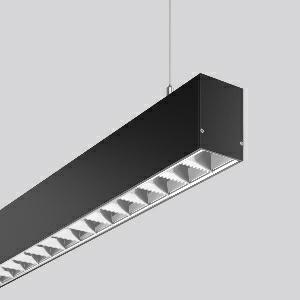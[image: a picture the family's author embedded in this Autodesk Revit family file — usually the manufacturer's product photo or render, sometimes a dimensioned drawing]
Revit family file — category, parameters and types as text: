
# Revit family: less_is_more_50_312338_003_1aff
name_source: partatom
category: Lighting Fixtures
units: mm (PartAtom-declared; Revit-internal decimal feet)

## family parameters
Cut with Voids When Loaded = No
Host = Face
Light Source = No
Part Type = Normal
Room Calculation Point = No
Round Connector Dimension = Use Diameter
Shared = No

## types (1)
- LESS IS MORE 50 (1 x LED Modul 830, 5050 lm, 3000)
    Apparent Load = 41 VA
    CIE Flux Codes = 95 100 100 100 100
    Color Rendering = 80
    Color Temperature = 3000
    Default Elevation = 1800 mm
    Description = Series: LESS IS MORE 50
Linear pendant luminaire for aesthetically sophisticated lighting. Housing: extruded aluminium profile, powder-coated. End cap aluminium powder-coated. Canopy made of aluminium, powder-coated. Alea optical system: Reflector structure (ABS, Aluminium-coated, highly polished) with integrated diffuser made of non-yellowing plastic (PMMA) opal for glare-free light at the workstation (screen-compliant according to EN 12464-1). Direct light emission. Suitable for pendant. 2-point steel cable suspension freely positionable and infinitely height-adjustable. Special lengths available on request. LED unit with integrated converter interchangeable and removable. Suitable for through-wiring. With sensors or as a safety luminaire on request. 
Colour: deep black, matt (RAL 9005)
Length: 1687 mm
Width: 57 mm
Height: 75 mm
Suspension length: 2000 mm
Lamp: LED
Socket: without socket
Colour temperature: 3000K
Colour rendering index (CRI): 80
System power: 41 W
Rated luminous flux: 5050 lm
Luminous efficiency: 123 lm/W
Control gear: Regulated power supply
Protection class: I
Type of protection: IP 20
    Height = 75 mm
    Lamp = 1 x LED Modul 830
    Lamp Light Flux = 5050 lm
    Lamp count = 1
    Length = 1687 mm
    Lifetime = 50000 h
    Luminous efficacy = 123 lm/W
    Manufacturer = RZB
    ModVariant = No
    Model = 312338.003
    Mounting Place = Ceiling
    Mounting Type = Pendant
    Number of Poles = 1
    OnlyDefault = Yes
    Power Factor = 1
    Product Name = LESS IS MORE 50
    Product group = Pendant LED linear luminaires
    ProductGroupID = 907
    Protection Class = Protection class I
    Protection Degree = IP 20
    RLX_Detail_Level = 1
    RLX_Emergency_Light_Flux = 0 lm
    RLX_Emergency_Type = 0
    RLX_Emergency_Type_DB = No
    RlxData = <blob elided: 39561 chars, md5=e01f24c3>
    Socket = socket
    Standby Power = 0 W
    System Light Flux = 5050 lm
    System Power = 41 W
    Type Comments = Product without accessories
    Type Image = 312342.003.jpg
    URL = http://relux.com
    VarID = ---
    Voltage = 230 V
    Voltage Range = 220-240 V
    Weight = 0.00 kg
    Width = 57 mm

## geometry (parser evidence)
native form markers: Blend x4, Sweep x11
no freeform markers — native parametric forms only
